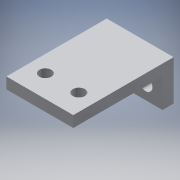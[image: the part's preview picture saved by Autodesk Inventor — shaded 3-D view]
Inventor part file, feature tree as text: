
AUTODESK INVENTOR PART (.ipt)
format: ipt  version: 2017 (Build 210142000, 142)  size: 126,976 bytes
history: native  units: in
note: dims shown in document units (in); Inventor stores cm internally (conversion verified against a paired STEP export)
features: sketch x3, hole x2, projected_geometry x2, extrude x1
ambient origin geometry x8: Origin, YZ Plane, XZ Plane, XY Plane, X Axis, Y Axis, Z Axis, Center Point
bodies: Solid1 (feature_tree)
feature tree (8):
  extrude  "Extrusion1"  Depth=1.125in
  hole  "Hole1"  [1 undecoded]
  hole  "Hole2"  [1 undecoded]
  sketch  "Sketch1"  dims[d0=0.45in d1=1.125in]
  sketch  "Sketch2"  dims[d2=0.325in d3=1.0in]
  projected_geometry  "Projected Loop1"
  sketch  "Sketch3"  dims[d4=0.75in d5=0.0in d6=0.375in d7=0.1875in d8=1.125in d11=0.135in d12=0.75in d13=0.375in d14=0.25in d15=0.5635in d16=1.0in d17=0.8108in d20=0.375in d21=0.1875in d22=0.1625in d23=0.1625in d24=0.15in d25=0.75in d26=0.375in d27=0.25in d28=0.5635in d29=1.0in d30=0.8108in d31=0.75in d32=0.75in d33=0.25in d34=0.25in d35=0.325in]
  projected_geometry  "Projected Loop2"
note: 2 required parameter values undecoded (feature->parameter linkage not recoverable at this tier; creation-order binding heuristic only, values carry confidence <= 0.55)
